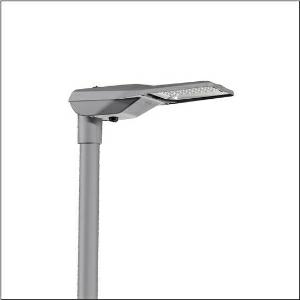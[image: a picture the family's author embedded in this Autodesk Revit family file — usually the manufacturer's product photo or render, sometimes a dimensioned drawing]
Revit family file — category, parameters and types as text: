
# Revit family: streetlight_sl_21_iq_mini___p0_8a_5xe2u31y08jb_ffd0
name_source: partatom
category: Lighting Fixtures
units: mm (PartAtom-declared; Revit-internal decimal feet)

## family parameters
Cut with Voids When Loaded = No
Host = Face
Light Source = No
Part Type = Normal
Room Calculation Point = No
Round Connector Dimension = Use Diameter
Shared = No

## types (1)
- --- (1 x LED, 11310 lm, 72.5 W, 3000K)
    Apparent Load = 73 VA
    CIE Flux Codes = 36 69 97 100 100
    Color Rendering = 70
    Color Temperature = 3000K
    Default Elevation = 1800 mm
    Description = Streetlight SL 21 iQ mini, mast luminaire, primary light control with lens, of PMMA, primary optical cover: cover, of toughened safety glass, transparent, light distribution: P0.8a, light emission: direct distribution, primary light characteristic: asymmetric, installation type: post-top, side-entry, LED, High Power LED, rated luminous flux: 11.310lm, luminous efficacy: 156lm/W, light colour: 730, colour temperature: 3000K, control gear: iQ-Street Remote, D4i with power reduction, control: pre-setting: logarithmic dimming characteristic, Street-Remote, Auto-Match, Temp-Guard, Lumen-Switch, Night-Set, Smart-Wire, Light-Fading, Desk-Remote (wireless, voltage-free reading and setting of iQ features in the workshop via application-optimized NFC function/RFID function), optimised constant luminous flux control (CLO 2.0), mains connection: 220..240V, AC, 50/60Hz, start of lifetime: 73W, end of service life: 76W, reduction: 33W, luminaire housing, of diecast aluminium, powder-coated, Siteco® metallic grey (DB 702S), corrosivity category C5 mid according to DIN EN ISO 12944, please order mast flange separately, inclination adjustable: 0°, 5°, 10°, 15°, sealing non-destructively replaceable, multi-level sealing system, length: 628mm, width: 235mm, height: 110mm, mast flange for spigot size: 42mm (side-entry): 5XC10008XM4, 60/48mm (side-entry/post-top): 5XC10108XM2, 76/60mm (side-entry/post-top): 5XC10108XM1, mounting height: 4..8m, Smart Interface below and above, protection rating (complete): IP66, insulation class (complete): insulation class II (safety insulation), certification: CE, ENEC, ENEC+, VDE, impact resistance: IK10, permissible operating ambient temperature for outdoor applications: -40..+50°C, standard-compliant lighting for roads and squares, packaging unit: 1 piece

Light Distribution: P0.8a
    Height = 110 mm
    Lamp = 1 x LED
    Lamp Light Flux = 11310 lm
    Lamp Power = 72.5 W
    Lamp count = 1
    Length = 625 mm
    Luminous efficacy = 156 lm/W
    Manufacturer = Siteco
    ModVariant = No
    Model = 5XE2U31Y08JB
    Number of Poles = 1
    OnlyDefault = Yes
    Power Factor = 1
    Product Name = Streetlight SL 21 iQ mini | P0.8a
    Product group = mast luminaire | pylon top
    ProductGroupID = 6100
    Protection Class = Protection class II
    Protection Degree = IP 66
    RLX_Detail_Level = 1
    RLX_Emergency_Light_Flux = 0 lm
    RLX_Emergency_Type = 0
    RLX_Emergency_Type_DB = No
    RlxData = <blob elided: 26425 chars, md5=0add3e9b>
    Socket = socket
    Standby Power = 0 W
    System Light Flux = 11310 lm
    System Power = 73 W
    Type Comments = factory setting: luminous flux: 100 % | dim-lin: 254 | 755 mA
    Type Image = l_1003514.jpg
    URL = http://relux.com
    VarID = @adj_072098
    Voltage = 0 V
    Weight = 0.00 kg
    Width = 234 mm

## geometry (parser evidence)
native form markers: Blend x4, Sweep x11
no freeform markers — native parametric forms only
